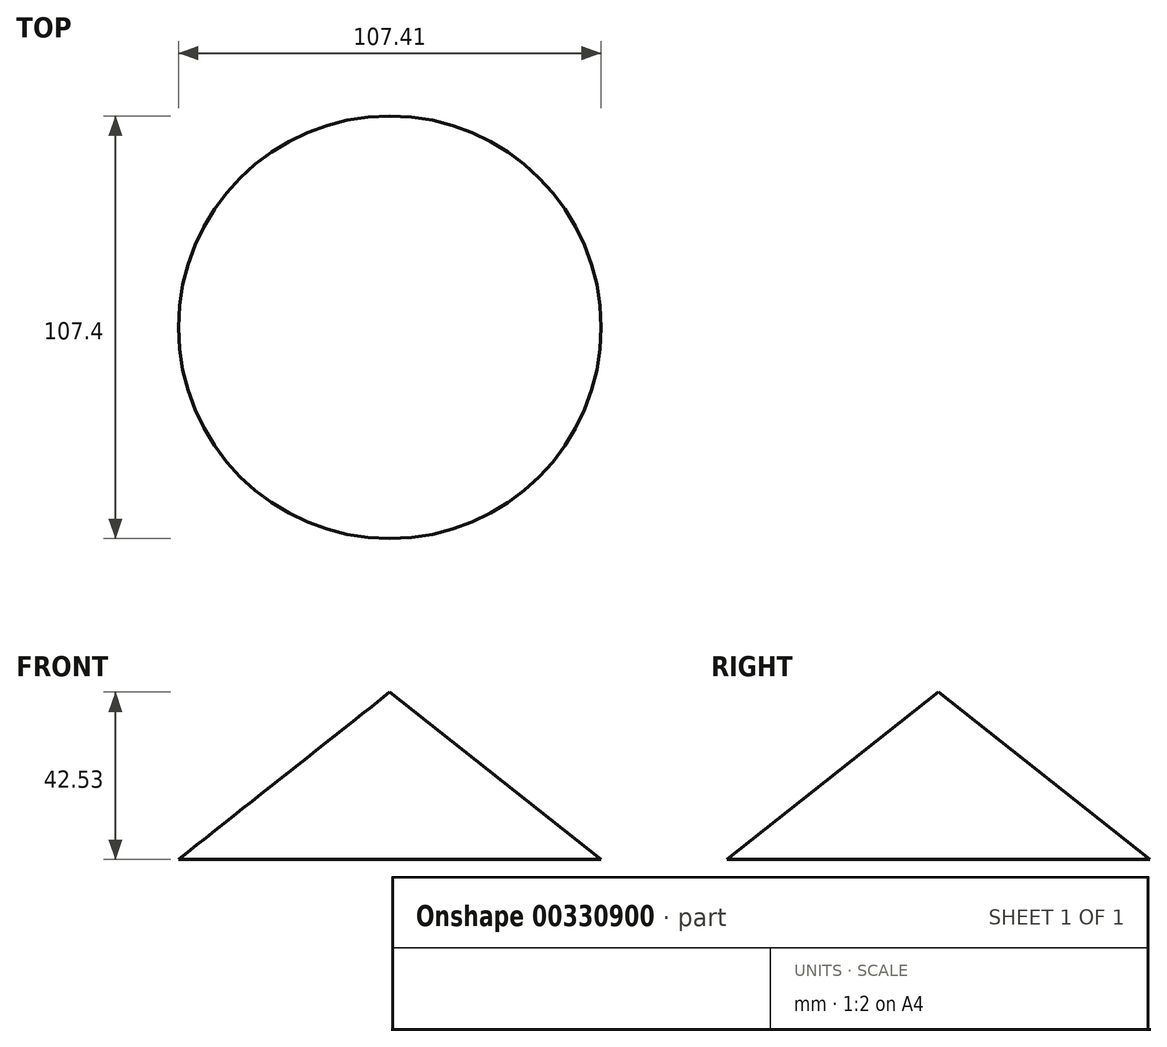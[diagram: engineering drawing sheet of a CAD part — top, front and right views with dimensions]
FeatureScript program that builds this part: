
annotation { "Feature Type Name" : "Feature", "Feature Type Description" : "" }
export const myFeature = defineFeature(function(context is Context, id is Id, definition is map)
    precondition{}
    {
        {
            var Q0;
            Q0=qCreatedBy(makeId("Front.planeOp"),FACE);
            var sketch = newSketch(context, id + "F0", { "sketchPlane" : qUnion([Q0])});
            skLineSegment(sketch, "E0", {"start": v(12.61, 33.7) * mm, "end": v(12.61, -8.83) * mm});
            skLineSegment(sketch, "E1", {"start": v(12.61, -8.83) * mm, "end": v(-41.09, -8.83) * mm});
            skLineSegment(sketch, "E2", {"start": v(-41.09, -8.83) * mm, "end": v(12.61, 33.7) * mm});
            skSolve(sketch);
        }
        {
            var Q0;
            Q0=makeQuery(id+"F0.imprint","IMPRINT",FACE,{"disambiguationData":[TD([[makeQuery(id+"F0.imprint","IMPRINT",EDGE,{"derivedFrom":sQuery(id+"F0.wireOp",EDGE,"E0")}),-1.0]])]});
            var Q1;
            Q1=sQuery(id+"F0.wireOp",EDGE,"E0");
            revolve(context, id + "F1", {"entities" : qUnion([Q0]), "axis" : qUnion([Q1]), "revolveType" : RevolveType.FULL});
        }
    });
